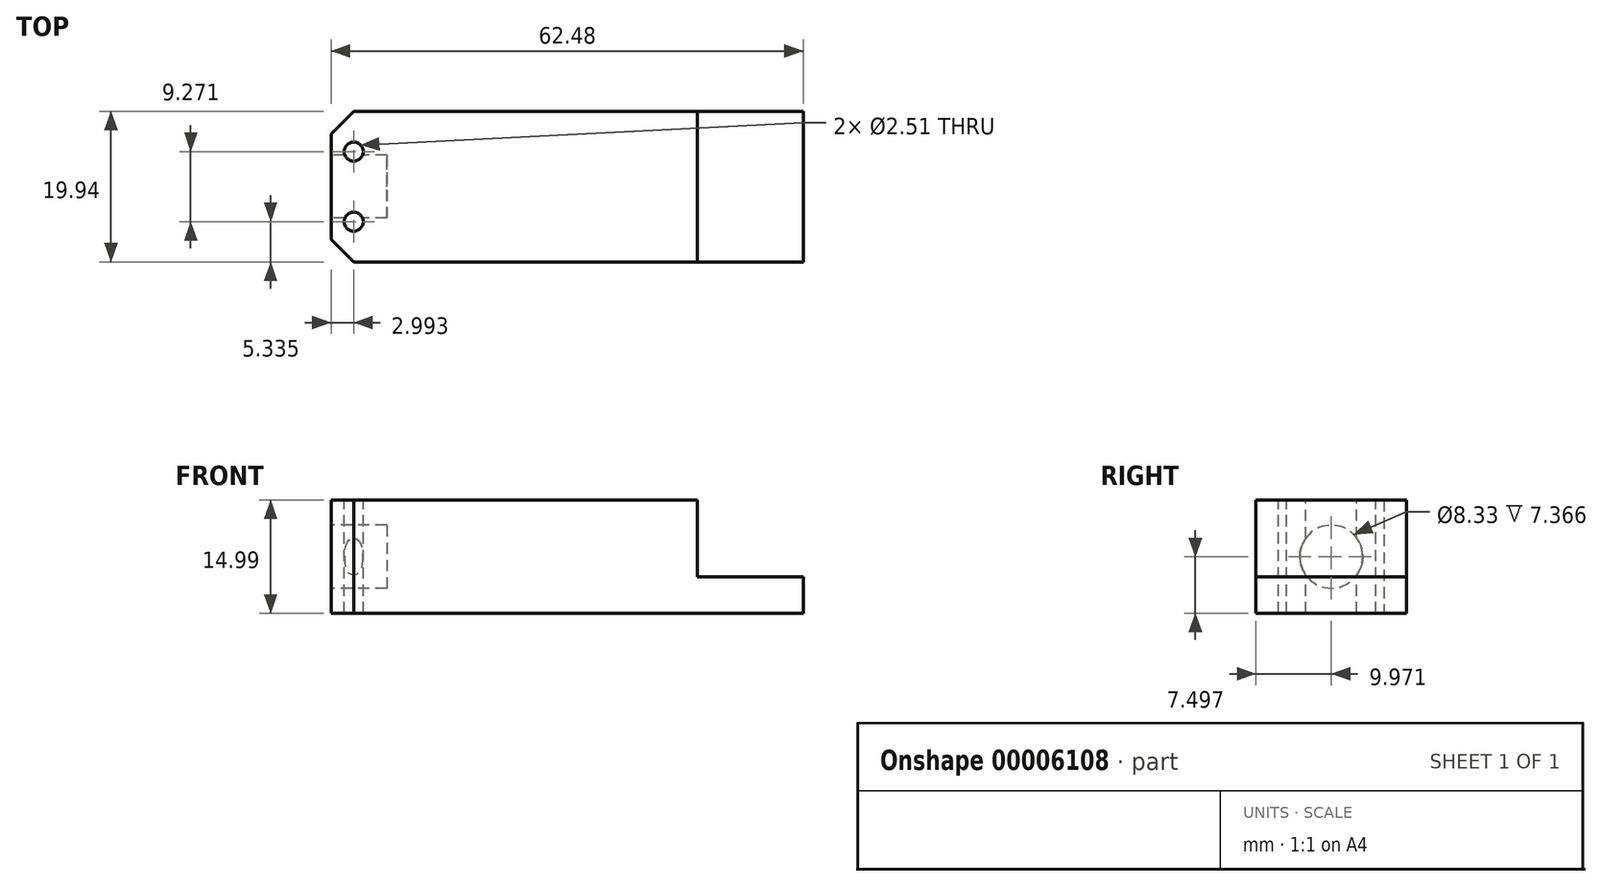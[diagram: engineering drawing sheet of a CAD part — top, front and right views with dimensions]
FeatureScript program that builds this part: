
annotation { "Feature Type Name" : "Feature", "Feature Type Description" : "" }
export const myFeature = defineFeature(function(context is Context, id is Id, definition is map)
    precondition{}
    {
        {
            var Q0;
            Q0=qCreatedBy(makeId("Front.planeOp"),FACE);
            var sketch = newSketch(context, id + "F0", { "sketchPlane" : qUnion([Q0])});
            skLineSegment(sketch, "E0", {"start": v(-14.02, 0) * mm, "end": v(-62.48, 0) * mm});
            skLineSegment(sketch, "E1", {"start": v(-62.48, 0) * mm, "end": v(-62.48, -14.99) * mm});
            skLineSegment(sketch, "E2", {"start": v(-62.48, -14.99) * mm, "end": v(0, -14.99) * mm});
            skLineSegment(sketch, "E3", {"start": v(0, -14.99) * mm, "end": v(0, -10.16) * mm});
            skLineSegment(sketch, "E4", {"start": v(0, -10.16) * mm, "end": v(-14.02, -10.16) * mm});
            skLineSegment(sketch, "E5", {"start": v(-14.02, -10.16) * mm, "end": v(-14.02, 0) * mm});
            skSolve(sketch);
        }
        {
            var Q0;
            Q0 = qSketchRegion(id + "F0", true);
            extrude(context, id + "F1", {"entities" : qUnion([Q0]), "depth" : 19.94 * mm});
        }
        {
            var Q0;
            Q0=makeQuery(id+"F1.opExtrude","SWEPT_FACE",FACE,{"disambiguationData":[OSD([sQuery(id+"F0.wireOp",EDGE,"E1")])]});
            var sketch = newSketch(context, id + "F2", { "sketchPlane" : qUnion([Q0])});
            skCircle(sketch, "E6", {"center": v(9.97, -7.5) * mm, "radius": 4.17 * mm});
            skSolve(sketch);
        }
        {
            var Q0;
            Q0 = qSketchRegion(id + "F2", true);
            extrude(context, id + "F3", {"entities" : qUnion([Q0]), "operationType" : NewBodyOperationType.REMOVE, "oppositeDirection" : true, "depth" : 7.37 * mm});
        }
        {
            var Q0;
            Q0=makeQuery(id+"F1.opExtrude","SWEPT_FACE",FACE,{"disambiguationData":[OSD([sQuery(id+"F0.wireOp",EDGE,"E0")])]});
            var sketch = newSketch(context, id + "F4", { "sketchPlane" : qUnion([Q0])});
            skCircle(sketch, "E7", {"center": v(-59.49, -5.33) * mm, "radius": 1.26 * mm});
            skCircle(sketch, "E8", {"center": v(-59.49, -14.6) * mm, "radius": 1.26 * mm});
            skSolve(sketch);
        }
        {
            var Q0;
            Q0 = qSketchRegion(id + "F4", true);
            extrude(context, id + "F5", {"entities" : qUnion([Q0]), "operationType" : NewBodyOperationType.REMOVE, "endBound" : BoundingType.THROUGH_ALL, "oppositeDirection" : true, "depth" : 25.4 * mm});
        }
        {
            var Q0;
            Q0=makeQuery(id+"F1.opExtrude","CAP_EDGE",EDGE,{"disambiguationData":[OSD([sQuery(id+"F0.wireOp",EDGE,"E1")])],"isStart":false});
            var Q1;
            Q1=makeQuery(id+"F1.opExtrude","CAP_EDGE",EDGE,{"disambiguationData":[OSD([sQuery(id+"F0.wireOp",EDGE,"E1")])],"isStart":true});
            chamfer(context, id + "F6", {"entities" : qUnion([Q0, Q1]), "width" : 3 * mm, "tangentPropagation" : true});
        }
    });
